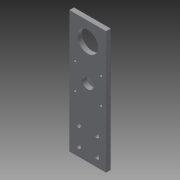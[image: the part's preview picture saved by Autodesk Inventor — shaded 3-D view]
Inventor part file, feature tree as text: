
AUTODESK INVENTOR PART (.ipt)
format: ipt  version: 2013 (Build 170138000, 138)  size: 199,680 bytes
history: native  units: in
note: dims shown in document units (in); Inventor stores cm internally (conversion verified against a paired STEP export)
features: extrude x10, sketch x10
ambient origin geometry x8: Origin, YZ Plane, XZ Plane, XY Plane, X Axis, Y Axis, Z Axis, Center Point
bodies: Solid1 (feature_tree)
feature tree (20):
  extrude  "Extrusion1"  Depth=6.688in
  extrude  "Extrusion2"  TaperAngle=90.0deg  [1 undecoded]
  extrude  "Extrusion3"  Depth=1.0in
  extrude  "Extrusion4"  Depth=2.0in
  extrude  "Extrusion5"  Depth=0.16in
  extrude  "Extrusion6"  Depth=0.16in
  extrude  "Extrusion7"  Depth=1.5in
  extrude  "Extrusion8"  TaperAngle=180.0deg  [1 undecoded]
  extrude  "Extrusion9"  TaperAngle=0.0deg  [1 undecoded]
  extrude  "Extrusion10"  Depth=0.25in
  sketch  "Sketch1"  dims[d0=2.0in d1=6.688in]
  sketch  "Sketch2"  dims[d2=1.0in d3=90.0deg]
  sketch  "Sketch3"  dims[d4=1.125in d5=1.0in]
  sketch  "Sketch4"  dims[d6=45.0deg d7=2.0in]
  sketch  "Sketch5"  dims[d9=0.16in d10=0.16in]
  sketch  "Sketch6"  dims[d11=0.16in d12=0.16in]
  sketch  "Sketch7"  dims[d13=2.0in d14=1.5in]
  sketch  "Sketch8"  dims[d15=0.5in d16=180.0deg]
  sketch  "Sketch9"  dims[d17=1.0in d18=0.0in]
  sketch  "Sketch10"  dims[d19=0.25in d20=0.25in d21=1.0in d22=0.0in d23=0.125in d24=0.125in d25=1.75in d26=0.75in d27=10.0in d28=0.0in d29=1.0in d30=1.0in d31=0.25in d32=0.25in d33=1.0in d34=0.0in d35=10.0in d36=0.0in d37=0.125in d38=0.0in d39=0.75in d40=0.25in d41=0.0in d43=2.938in d44=90.0deg d45=0.625in d46=1.0in d47=0.0in d48=1.125in d49=1.0in d50=0.0in d51=1.0in d52=45.0deg d53=2.0in d54=0.0in d55=0.16in d56=0.16in d57=0.16in d58=0.16in d59=0.25in d60=0.0in d61=0.25in d62=0.0in]
note: 3 required parameter values undecoded (feature->parameter linkage not recoverable at this tier; creation-order binding heuristic only, values carry confidence <= 0.55)
